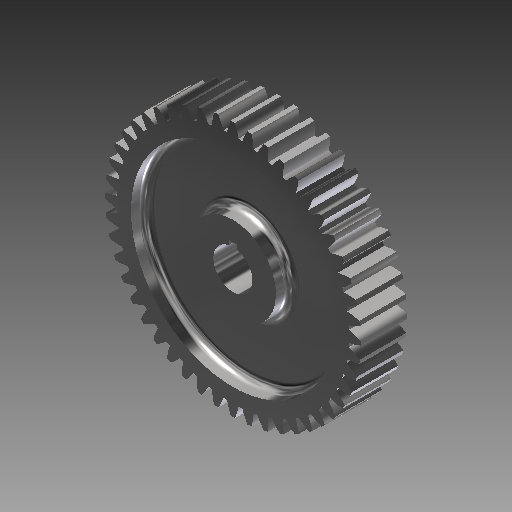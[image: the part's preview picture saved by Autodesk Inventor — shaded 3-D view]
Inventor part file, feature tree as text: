
AUTODESK INVENTOR PART (.ipt)
format: ipt  version: 2020 (Build 240168000, 168)  size: 486,912 bytes
history: native  units: mm (DEFAULTED — no unit token found)
features: plane x4, sketch x4, other x3, extrude x2, revolve x1, hole x1
ambient origin geometry x8: Origin, YZ Plane, XZ Plane, XY Plane, X Axis, Y Axis, Z Axis, Center Point
bodies: Solid1 (feature_tree)
feature tree (15):
  extrude  "Extrusion1"  Depth=18.796mm TaperAngle=0.0deg
  plane  "Work Plane1"
  plane  "Work Plane2"
  plane  "Work Plane3"
  other  "Spur Gear"
  plane  "Work Plane4"
  revolve  "Revolution1"  [1 undecoded]
  hole  "Hole1"  [1 undecoded]
  extrude  "Extrusion2"  TaperAngle=0.0deg  [1 undecoded]
  sketch  "Sketch1"  dims[d0=103.706793mm d1=18.796mm d2=0.0mm]
  sketch  "Sketch2"  dims[d3=101.930768mm d4=76.2mm d5=0.0mm]
  other  "Srf1"
  sketch  "Sketch3"  dims[d6=0.0mm d7=0.654498mm d9=0.0mm]
  sketch  "Sketch4"  dims[d14=0.0mm d15=63.70673mm d16=0.0mm d17=0.0mm d18=0.0mm d19=63.70673mm d20=82.55mm d21=34.925mm d22=0.0mm d23=6.35mm d24=3.175mm d25=90.0deg d26=25.4mm d27=25.4mm d28=15.8623mm d29=19.05mm d30=9.525mm d31=6.35mm d32=14.3117mm d33=25.4mm d34=20.594885mm d35=3.175mm d36=1.5875mm d37=1.5875mm d38=3.175mm d39=25.4mm d40=0.0mm]
  other  "Pitch Diameter"
note: 3 required parameter values undecoded (feature->parameter linkage not recoverable at this tier; creation-order binding heuristic only, values carry confidence <= 0.55)